# Revit family: BIM_NetShelter_SX_Series_Rack_Enclosure_21-jun-21
name_source: partatom
category: Mechanical Equipment
revit_build: Autodesk Revit 2016 (Build: 20150220_1215(x64)
units: mm (PartAtom-declared; Revit-internal decimal feet)

## family parameters
Always vertical = Yes
Cut with Voids When Loaded = No
OmniClass Number = 23.75.00.00
OmniClass Title = Climate Control (HVAC)
Part Type = Normal
Room Calculation Point = No
Round Connector Dimension = Use Diameter
Shared = No
Work Plane-Based = No

## types (28) — shared parameters
BS L5 = 774 mm
BS-L3 = 532 mm
Description = Racks and Enclosures
Front Clearance = 1000 mm  [stored 3.28084 ft]
Manufacturer = Schneider-electric
Manufacturer URL = http://www.schneider-electric.com
Model = NetShelter SX
Rear Clearance = 1000 mm  [stored 3.28084 ft]
Slot 3 = No
Top Clearance = 600 mm  [stored 1.9685 ft]
zero-valued in all types: Default Elevation

## per-type parameters (varying)
- AR3100 - NetShelter SX, 42U, 600mm Wide X 1070mm Depth: Centre Slot=Yes; Cut ref=55 mm  [stored 0.180446 ft]; Cutout 1=Yes; Cutout 2=No; Cutout Distance=590 mm  [stored 1.9357 ft]; Cutout Height=117 mm  [stored 0.383858 ft]; Cutout Width=155 mm  [stored 0.50853 ft]; Door=1911 mm; Door Radius=1419 mm; Door Width L1=431 mm  [stored 1.41404 ft]; Door1=1911 mm; Foot to Foot-H=570 mm; Foot to Foot-V=1023 mm; Handle to Handle=1092 mm; Height=1991 mm; Length=1070 mm; Net Weight of Unit=125.00 kg; Number of Small Slots L1=20; Number of small Slots L2=20; OSSS-L1=700 mm  [stored 2.29659 ft]; OSSS-L2=698 mm  [stored 2.29003 ft]; Product URL=https://www.apc.com; Side Posts=1955 mm; Slot 1=Yes; Slot 2=No; Top Roof=892 mm  [stored 2.92651 ft]; URL=http://www.schneider-electric.com; W to W-H=358 mm  [stored 1.17454 ft]; Wheel to Wheel-V=941 mm  [stored 3.08727 ft]; Width=600 mm  [stored 1.9685 ft]
- AR3307 - NetShelter SX, 48U, 600mm Wide X 1200mm Depth: Centre Slot=Yes; Cut ref=55 mm  [stored 0.180446 ft]; Cutout 1=Yes; Cutout 2=No; Cutout Distance=640 mm  [stored 2.09974 ft]; Cutout Height=200 mm  [stored 0.656168 ft]; Cutout Width=117 mm  [stored 0.383858 ft]; Door=2178 mm; Door Radius=1420 mm; Door Width L1=431 mm  [stored 1.41404 ft]; Door1=2178 mm; Foot to Foot-H=570 mm; Foot to Foot-V=1154 mm; Handle to Handle=1222 mm; Height=2258 mm; Length=1200 mm; Net Weight of Unit=149.55 kg; Number of Small Slots L1=21; Number of small Slots L2=28; OSSS-L1=760 mm; OSSS-L2=986 mm  [stored 3.23491 ft]; Product URL=https://www.apc.com; Side Posts=2222 mm; Slot 1=Yes; Slot 2=Yes; Top Roof=1021 mm  [stored 3.34974 ft]; URL=http://www.schneider-electric.com; W to W-H=358 mm  [stored 1.17454 ft]; Wheel to Wheel-V=1072 mm; Width=600 mm  [stored 1.9685 ft]
- AR3150 - NetShelter SX, 42U, 750mm Wide X 1070mm Depth: Centre Slot=Yes; Cut ref=55 mm  [stored 0.180446 ft]; Cutout 1=Yes; Cutout 2=No; Cutout Distance=600 mm  [stored 1.9685 ft]; Cutout Height=117 mm  [stored 0.383858 ft]; Cutout Width=155 mm  [stored 0.50853 ft]; Door=1911 mm; Door Radius=2586 mm; Door Width L1=581 mm  [stored 1.90617 ft]; Door1=1911 mm; Foot to Foot-H=720 mm  [stored 2.3622 ft]; Foot to Foot-V=1023 mm; Handle to Handle=1092 mm; Height=1991 mm; Length=1070 mm; Net Weight of Unit=138.23 kg; Number of Small Slots L1=20; Number of small Slots L2=20; OSSS-L1=698 mm  [stored 2.29003 ft]; OSSS-L2=840 mm  [stored 2.75591 ft]; Product URL=https://www.apc.com; Side Posts=1955 mm; Slot 1=Yes; Slot 2=No; Top Roof=892 mm  [stored 2.92651 ft]; URL=http://www.schneider-electric.com; W to W-H=508 mm; Wheel to Wheel-V=941 mm  [stored 3.08727 ft]; Width=750 mm  [stored 2.46063 ft]
- AR3105 - NetShelter SX, 45U, 600mm Wide X 1070mm Depth: Centre Slot=Yes; Cut ref=55 mm  [stored 0.180446 ft]; Cutout 1=Yes; Cutout 2=No; Cutout Distance=600 mm  [stored 1.9685 ft]; Cutout Height=117 mm  [stored 0.383858 ft]; Cutout Width=155 mm  [stored 0.50853 ft]; Door=2044 mm; Door Radius=1419 mm; Door Width L1=431 mm  [stored 1.41404 ft]; Door1=2044 mm; Foot to Foot-H=570 mm; Foot to Foot-V=1023 mm; Handle to Handle=1092 mm; Height=2124 mm; Length=1070 mm; Net Weight of Unit=137.00 kg; Number of Small Slots L1=20; Number of small Slots L2=20; OSSS-L1=693 mm  [stored 2.27362 ft]; OSSS-L2=698 mm  [stored 2.29003 ft]; Product URL=https://www.apc.com; Side Posts=2088 mm; Slot 1=Yes; Slot 2=No; Top Roof=892 mm  [stored 2.92651 ft]; URL=http://www.schneider-electric.com; W to W-H=358 mm  [stored 1.17454 ft]; Wheel to Wheel-V=941 mm  [stored 3.08727 ft]; Width=600 mm  [stored 1.9685 ft]
- AR3140 - NetShelter SX, 42U, 750mm Wide X 1070mm Depth: Centre Slot=No; Cut ref=1 mm  [stored 0.00328084 ft]; Cutout 1=No; Cutout 2=Yes; Cutout Distance=423 mm  [stored 1.3878 ft]; Cutout Height=117 mm  [stored 0.383858 ft]; Cutout Width=142 mm  [stored 0.465879 ft]; Door=1911 mm; Door Radius=2586 mm; Door Width L1=581 mm  [stored 1.90617 ft]; Door1=1911 mm; Foot to Foot-H=720 mm  [stored 2.3622 ft]; Foot to Foot-V=1023 mm; Handle to Handle=1092 mm; Height=1991 mm; Length=1070 mm; Net Weight of Unit=156.00 kg; Number of Small Slots L1=20; Number of small Slots L2=20; OSSS-L1=825 mm  [stored 2.70669 ft]; OSSS-L2=825 mm  [stored 2.70669 ft]; Product URL=https://www.apc.com; Side Posts=1955 mm; Slot 1=No; Slot 2=No; Top Roof=892 mm  [stored 2.92651 ft]; URL=http://www.schneider-electric.com; W to W-H=508 mm; Wheel to Wheel-V=941 mm  [stored 3.08727 ft]; Width=750 mm  [stored 2.46063 ft]
- AR3155 - NetShelter SX, 45U, 750mm Wide X 1070mm Depth: Centre Slot=Yes; Cut ref=55 mm  [stored 0.180446 ft]; Cutout 1=Yes; Cutout 2=No; Cutout Distance=600 mm  [stored 1.9685 ft]; Cutout Height=117 mm  [stored 0.383858 ft]; Cutout Width=155 mm  [stored 0.50853 ft]; Door=2044 mm; Door Radius=2586 mm; Door Width L1=581 mm  [stored 1.90617 ft]; Door1=2044 mm; Foot to Foot-H=720 mm  [stored 2.3622 ft]; Foot to Foot-V=1023 mm; Handle to Handle=1092 mm; Height=2124 mm; Length=1070 mm; Net Weight of Unit=155.00 kg; Number of Small Slots L1=20; Number of small Slots L2=20; OSSS-L1=710 mm; OSSS-L2=850 mm  [stored 2.78871 ft]; Product URL=https://www.apc.com; Side Posts=2088 mm; Slot 1=Yes; Slot 2=No; Top Roof=892 mm  [stored 2.92651 ft]; URL=http://www.schneider-electric.com; W to W-H=508 mm; Wheel to Wheel-V=941 mm  [stored 3.08727 ft]; Width=750 mm  [stored 2.46063 ft]
- AR3107 - NetShelter SX, 48U, 600mm Wide X 1070mm Depth: Centre Slot=Yes; Cut ref=55 mm  [stored 0.180446 ft]; Cutout 1=Yes; Cutout 2=No; Cutout Distance=600 mm  [stored 1.9685 ft]; Cutout Height=117 mm  [stored 0.383858 ft]; Cutout Width=155 mm  [stored 0.50853 ft]; Door=2178 mm; Door Radius=1419 mm; Door Width L1=431 mm  [stored 1.41404 ft]; Door1=2178 mm; Foot to Foot-H=570 mm; Foot to Foot-V=1023 mm; Handle to Handle=1092 mm; Height=2258 mm; Length=1070 mm; Net Weight of Unit=138.23 kg; Number of Small Slots L1=20; Number of small Slots L2=20; OSSS-L1=693 mm  [stored 2.27362 ft]; OSSS-L2=698 mm  [stored 2.29003 ft]; Product URL=https://www.apc.com; Side Posts=2222 mm; Slot 1=Yes; Slot 2=No; Top Roof=892 mm  [stored 2.92651 ft]; URL=http://www.schneider-electric.com; W to W-H=358 mm  [stored 1.17454 ft]; Wheel to Wheel-V=941 mm  [stored 3.08727 ft]; Width=600 mm  [stored 1.9685 ft]
- AR3157SP - NetShelter SX, 48U, 750mm Wide X 1070mm Depth: Centre Slot=Yes; Cut ref=55 mm  [stored 0.180446 ft]; Cutout 1=Yes; Cutout 2=No; Cutout Distance=600 mm  [stored 1.9685 ft]; Cutout Height=117 mm  [stored 0.383858 ft]; Cutout Width=155 mm  [stored 0.50853 ft]; Door=2178 mm; Door Radius=2586 mm; Door Width L1=581 mm  [stored 1.90617 ft]; Door1=2178 mm; Foot to Foot-H=720 mm  [stored 2.3622 ft]; Foot to Foot-V=1023 mm; Handle to Handle=1092 mm; Height=2258 mm; Length=1070 mm; Net Weight of Unit=169.00 kg; Number of Small Slots L1=20; Number of small Slots L2=20; OSSS-L1=710 mm; OSSS-L2=850 mm  [stored 2.78871 ft]; Product URL=https://www.apc.com; Side Posts=2222 mm; Slot 1=Yes; Slot 2=No; Top Roof=892 mm  [stored 2.92651 ft]; URL=http://www.schneider-electric.com; W to W-H=508 mm; Wheel to Wheel-V=941 mm  [stored 3.08727 ft]; Width=750 mm  [stored 2.46063 ft]
- AR3300 - NetShelter SX, 42U, 600mm Wide X 1200mm Depth: Centre Slot=Yes; Cut ref=55 mm  [stored 0.180446 ft]; Cutout 1=Yes; Cutout 2=No; Cutout Distance=640 mm  [stored 2.09974 ft]; Cutout Height=200 mm  [stored 0.656168 ft]; Cutout Width=117 mm  [stored 0.383858 ft]; Door=1911 mm; Door Radius=1420 mm; Door Width L1=431 mm  [stored 1.41404 ft]; Door1=1911 mm; Foot to Foot-H=570 mm; Foot to Foot-V=1154 mm; Handle to Handle=1222 mm; Height=1991 mm; Length=1200 mm; Net Weight of Unit=134.00 kg; Number of Small Slots L1=21; Number of small Slots L2=28; OSSS-L1=760 mm; OSSS-L2=986 mm  [stored 3.23491 ft]; Product URL=https://www.apc.com; Side Posts=1955 mm; Slot 1=Yes; Slot 2=Yes; Top Roof=1021 mm  [stored 3.34974 ft]; URL=http://www.schneider-electric.com; W to W-H=358 mm  [stored 1.17454 ft]; Wheel to Wheel-V=1072 mm; Width=600 mm  [stored 1.9685 ft]
- AR3305 - NetShelter SX, 45U, 600mm Wide X 1200mm Depth: Centre Slot=Yes; Cut ref=55 mm  [stored 0.180446 ft]; Cutout 1=Yes; Cutout 2=No; Cutout Distance=640 mm  [stored 2.09974 ft]; Cutout Height=200 mm  [stored 0.656168 ft]; Cutout Width=117 mm  [stored 0.383858 ft]; Door=2044 mm; Door Radius=1420 mm; Door Width L1=431 mm  [stored 1.41404 ft]; Door1=2044 mm; Foot to Foot-H=570 mm; Foot to Foot-V=1154 mm; Handle to Handle=1222 mm; Height=2124 mm; Length=1200 mm; Net Weight of Unit=141.00 kg; Number of Small Slots L1=21; Number of small Slots L2=28; OSSS-L1=760 mm; OSSS-L2=986 mm  [stored 3.23491 ft]; Product URL=https://www.apc.com; Side Posts=2088 mm; Slot 1=Yes; Slot 2=Yes; Top Roof=1021 mm  [stored 3.34974 ft]; URL=http://www.schneider-electric.com; W to W-H=358 mm  [stored 1.17454 ft]; Wheel to Wheel-V=1072 mm; Width=600 mm  [stored 1.9685 ft]
- AR3340 - NetShelter SX, 42U, 750mm Wide X 1200mm Depth: Centre Slot=No; Cut ref=1 mm  [stored 0.00328084 ft]; Cutout 1=No; Cutout 2=Yes; Cutout Distance=428 mm  [stored 1.4042 ft]; Cutout Height=240 mm  [stored 0.787402 ft]; Cutout Width=145 mm  [stored 0.475722 ft]; Door=1911 mm; Door Radius=2586 mm; Door Width L1=581 mm  [stored 1.90617 ft]; Door1=1911 mm; Foot to Foot-H=720 mm  [stored 2.3622 ft]; Foot to Foot-V=1154 mm; Handle to Handle=1222 mm; Height=1991 mm; Length=1200 mm; Net Weight of Unit=161.40 kg; Number of Small Slots L1=28; Number of small Slots L2=28; OSSS-L1=986 mm  [stored 3.23491 ft]; OSSS-L2=986 mm  [stored 3.23491 ft]; Product URL=https://www.apc.com; Side Posts=1955 mm; Slot 1=No; Slot 2=No; Top Roof=1021 mm  [stored 3.34974 ft]; URL=http://www.schneider-electric.com; W to W-H=508 mm; Wheel to Wheel-V=1072 mm; Width=750 mm  [stored 2.46063 ft]
- AR3350 - NetShelter SX, 42U, 750mm Wide X 1200mm Depth: Centre Slot=Yes; Cut ref=55 mm  [stored 0.180446 ft]; Cutout 1=Yes; Cutout 2=No; Cutout Distance=640 mm  [stored 2.09974 ft]; Cutout Height=200 mm  [stored 0.656168 ft]; Cutout Width=117 mm  [stored 0.383858 ft]; Door=1911 mm; Door Radius=2586 mm; Door Width L1=581 mm  [stored 1.90617 ft]; Door1=1911 mm; Foot to Foot-H=720 mm  [stored 2.3622 ft]; Foot to Foot-V=1154 mm; Handle to Handle=1222 mm; Height=1991 mm; Length=1200 mm; Net Weight of Unit=161.40 kg; Number of Small Slots L1=28; Number of small Slots L2=28; OSSS-L1=986 mm  [stored 3.23491 ft]; OSSS-L2=986 mm  [stored 3.23491 ft]; Product URL=https://www.apc.com; Side Posts=1955 mm; Slot 1=Yes; Slot 2=Yes; Top Roof=1021 mm  [stored 3.34974 ft]; URL=http://www.schneider-electric.com; W to W-H=508 mm; Wheel to Wheel-V=1072 mm; Width=750 mm  [stored 2.46063 ft]
- AR3355 - NetShelter SX, 45U, 750mm Wide X 1200mm Depth: Centre Slot=Yes; Cut ref=55 mm  [stored 0.180446 ft]; Cutout 1=Yes; Cutout 2=No; Cutout Distance=640 mm  [stored 2.09974 ft]; Cutout Height=200 mm  [stored 0.656168 ft]; Cutout Width=117 mm  [stored 0.383858 ft]; Door=2044 mm; Door Radius=2586 mm; Door Width L1=581 mm  [stored 1.90617 ft]; Door1=2044 mm; Foot to Foot-H=720 mm  [stored 2.3622 ft]; Foot to Foot-V=1154 mm; Handle to Handle=1222 mm; Height=2124 mm; Length=1200 mm; Net Weight of Unit=169.00 kg; Number of Small Slots L1=28; Number of small Slots L2=28; OSSS-L1=986 mm  [stored 3.23491 ft]; OSSS-L2=986 mm  [stored 3.23491 ft]; Product URL=https://www.apc.com; Side Posts=2088 mm; Slot 1=Yes; Slot 2=Yes; Top Roof=1021 mm  [stored 3.34974 ft]; URL=http://www.schneider-electric.com; W to W-H=508 mm; Wheel to Wheel-V=1072 mm; Width=750 mm  [stored 2.46063 ft]
- AR3347 - NetShelter SX, 48U, 750mm Wide X 1200mm Depth: Centre Slot=No; Cut ref=1 mm  [stored 0.00328084 ft]; Cutout 1=No; Cutout 2=Yes; Cutout Distance=428 mm  [stored 1.4042 ft]; Cutout Height=240 mm  [stored 0.787402 ft]; Cutout Width=145 mm  [stored 0.475722 ft]; Door=2178 mm; Door Radius=2586 mm; Door Width L1=581 mm  [stored 1.90617 ft]; Door1=2178 mm; Foot to Foot-H=720 mm  [stored 2.3622 ft]; Foot to Foot-V=1154 mm; Handle to Handle=1222 mm; Height=2258 mm; Length=1200 mm; Net Weight of Unit=185.00 kg; Number of Small Slots L1=28; Number of small Slots L2=28; OSSS-L1=986 mm  [stored 3.23491 ft]; OSSS-L2=986 mm  [stored 3.23491 ft]; Product URL=https://www.apc.com; Side Posts=2222 mm; Slot 1=No; Slot 2=No; Top Roof=1021 mm  [stored 3.34974 ft]; URL=http://www.schneider-electric.com; W to W-H=508 mm; Wheel to Wheel-V=1072 mm; Width=750 mm  [stored 2.46063 ft]
- AR3357 - NetShelter SX, 48U, 750mm Wide X 1200mm Depth: Centre Slot=Yes; Cut ref=55 mm  [stored 0.180446 ft]; Cutout 1=Yes; Cutout 2=No; Cutout Distance=640 mm  [stored 2.09974 ft]; Cutout Height=200 mm  [stored 0.656168 ft]; Cutout Width=117 mm  [stored 0.383858 ft]; Door=2178 mm; Door Radius=2586 mm; Door Width L1=581 mm  [stored 1.90617 ft]; Door1=2178 mm; Foot to Foot-H=720 mm  [stored 2.3622 ft]; Foot to Foot-V=1154 mm; Handle to Handle=1222 mm; Height=2258 mm; Length=1200 mm; Net Weight of Unit=169.00 kg; Number of Small Slots L1=28; Number of small Slots L2=28; OSSS-L1=986 mm  [stored 3.23491 ft]; OSSS-L2=986 mm  [stored 3.23491 ft]; Product URL=https://www.apc.com; Side Posts=2222 mm; Slot 1=Yes; Slot 2=Yes; Top Roof=1021 mm  [stored 3.34974 ft]; URL=http://www.schneider-electric.com; W to W-H=508 mm; Wheel to Wheel-V=1072 mm; Width=750 mm  [stored 2.46063 ft]
- AR3380G - NetShelter SX, 42U, 800mm Wide X 1200mm Depth: Centre Slot=Yes; Cut ref=55 mm  [stored 0.180446 ft]; Cutout 1=Yes; Cutout 2=No; Cutout Distance=640 mm  [stored 2.09974 ft]; Cutout Height=210 mm  [stored 0.688976 ft]; Cutout Width=117 mm  [stored 0.383858 ft]; Door=1911 mm; Door Radius=3048 mm; Door Width L1=631 mm  [stored 2.07021 ft]; Door1=1911 mm; Foot to Foot-H=720 mm  [stored 2.3622 ft]; Foot to Foot-V=1154 mm; Handle to Handle=1222 mm; Height=1991 mm; Length=1200 mm; Net Weight of Unit=181.50 kg; Number of Small Slots L1=28; Number of small Slots L2=28; OSSS-L1=986 mm  [stored 3.23491 ft]; OSSS-L2=986 mm  [stored 3.23491 ft]; Side Posts=1955 mm; Slot 1=Yes; Slot 2=Yes; Top Roof=1021 mm  [stored 3.34974 ft]; URL=http://www.schneider-electric.com; W to W-H=642 mm  [stored 2.1063 ft]; Wheel to Wheel-V=1072 mm; Width=800 mm  [stored 2.62467 ft]
- AR3155SP - NetShelter SX, 45U, 750mm Wide X 1070mm Depth: Centre Slot=Yes; Cut ref=55 mm  [stored 0.180446 ft]; Cutout 1=Yes; Cutout 2=No; Cutout Distance=600 mm  [stored 1.9685 ft]; Cutout Height=117 mm  [stored 0.383858 ft]; Cutout Width=155 mm  [stored 0.50853 ft]; Door=2044 mm; Door Radius=2586 mm; Door Width L1=581 mm  [stored 1.90617 ft]; Door1=2044 mm; Foot to Foot-H=720 mm  [stored 2.3622 ft]; Foot to Foot-V=1023 mm; Handle to Handle=1092 mm; Height=2124 mm; Length=1070 mm; Net Weight of Unit=155.00 kg; Number of Small Slots L1=20; Number of small Slots L2=20; OSSS-L1=710 mm; OSSS-L2=850 mm  [stored 2.78871 ft]; Side Posts=2088 mm; Slot 1=Yes; Slot 2=No; Top Roof=892 mm  [stored 2.92651 ft]; URL=http://www.schneider-electric.com; W to W-H=508 mm; Wheel to Wheel-V=941 mm  [stored 3.08727 ft]; Width=750 mm  [stored 2.46063 ft]
- AR3157 - NetShelter SX, 48U, 750mm Wide X 1070mm Depth: Centre Slot=Yes; Cut ref=55 mm  [stored 0.180446 ft]; Cutout 1=Yes; Cutout 2=No; Cutout Distance=600 mm  [stored 1.9685 ft]; Cutout Height=117 mm  [stored 0.383858 ft]; Cutout Width=155 mm  [stored 0.50853 ft]; Door=2178 mm; Door Radius=2586 mm; Door Width L1=581 mm  [stored 1.90617 ft]; Door1=2178 mm; Foot to Foot-H=720 mm  [stored 2.3622 ft]; Foot to Foot-V=1023 mm; Handle to Handle=1092 mm; Height=2258 mm; Length=1070 mm; Net Weight of Unit=169.00 kg; Number of Small Slots L1=20; Number of small Slots L2=20; OSSS-L1=710 mm; OSSS-L2=850 mm  [stored 2.78871 ft]; Product URL=https://www.apc.com; Side Posts=2222 mm; Slot 1=Yes; Slot 2=No; Top Roof=892 mm  [stored 2.92651 ft]; URL=http://www.schneider-electric.com; W to W-H=508 mm; Wheel to Wheel-V=941 mm  [stored 3.08727 ft]; Width=750 mm  [stored 2.46063 ft]
- AR3100SP - NetShelter SX, 42U, 600mm Wide X 1070mm Depth: Centre Slot=Yes; Cut ref=55 mm  [stored 0.180446 ft]; Cutout 1=Yes; Cutout 2=No; Cutout Distance=590 mm  [stored 1.9357 ft]; Cutout Height=117 mm  [stored 0.383858 ft]; Cutout Width=155 mm  [stored 0.50853 ft]; Door=1911 mm; Door Radius=1419 mm; Door Width L1=431 mm  [stored 1.41404 ft]; Door1=1911 mm; Foot to Foot-H=570 mm; Foot to Foot-V=1023 mm; Handle to Handle=1092 mm; Height=1991 mm; Length=1070 mm; Net Weight of Unit=125.00 kg; Number of Small Slots L1=20; Number of small Slots L2=20; OSSS-L1=700 mm  [stored 2.29659 ft]; OSSS-L2=698 mm  [stored 2.29003 ft]; Product URL=https://www.apc.com; Side Posts=1955 mm; Slot 1=Yes; Slot 2=No; Top Roof=892 mm  [stored 2.92651 ft]; URL=http://www.schneider-electric.com; W to W-H=358 mm  [stored 1.17454 ft]; Wheel to Wheel-V=941 mm  [stored 3.08727 ft]; Width=600 mm  [stored 1.9685 ft]
- AR3105SP - NetShelter SX, 45U, 600mm Wide X 1070mm Depth: Centre Slot=Yes; Cut ref=55 mm  [stored 0.180446 ft]; Cutout 1=Yes; Cutout 2=No; Cutout Distance=600 mm  [stored 1.9685 ft]; Cutout Height=117 mm  [stored 0.383858 ft]; Cutout Width=155 mm  [stored 0.50853 ft]; Door=2044 mm; Door Radius=1419 mm; Door Width L1=431 mm  [stored 1.41404 ft]; Door1=2044 mm; Foot to Foot-H=570 mm; Foot to Foot-V=1023 mm; Handle to Handle=1092 mm; Height=2124 mm; Length=1070 mm; Net Weight of Unit=137.00 kg; Number of Small Slots L1=20; Number of small Slots L2=20; OSSS-L1=693 mm  [stored 2.27362 ft]; OSSS-L2=698 mm  [stored 2.29003 ft]; Side Posts=2088 mm; Slot 1=Yes; Slot 2=No; Top Roof=892 mm  [stored 2.92651 ft]; URL=http://www.schneider-electric.com; W to W-H=358 mm  [stored 1.17454 ft]; Wheel to Wheel-V=941 mm  [stored 3.08727 ft]; Width=600 mm  [stored 1.9685 ft]
- AR3107SP - NetShelter SX, 48U, 600mm Wide X 1070mm Depth: Centre Slot=Yes; Cut ref=55 mm  [stored 0.180446 ft]; Cutout 1=Yes; Cutout 2=No; Cutout Distance=600 mm  [stored 1.9685 ft]; Cutout Height=117 mm  [stored 0.383858 ft]; Cutout Width=155 mm  [stored 0.50853 ft]; Door=2178 mm; Door Radius=1419 mm; Door Width L1=431 mm  [stored 1.41404 ft]; Door1=2178 mm; Foot to Foot-H=570 mm; Foot to Foot-V=1023 mm; Handle to Handle=1092 mm; Height=2258 mm; Length=1070 mm; Net Weight of Unit=138.23 kg; Number of Small Slots L1=20; Number of small Slots L2=20; OSSS-L1=693 mm  [stored 2.27362 ft]; OSSS-L2=698 mm  [stored 2.29003 ft]; Product URL=https://www.apc.com; Side Posts=2222 mm; Slot 1=Yes; Slot 2=No; Top Roof=892 mm  [stored 2.92651 ft]; URL=http://www.schneider-electric.com; W to W-H=358 mm  [stored 1.17454 ft]; Wheel to Wheel-V=941 mm  [stored 3.08727 ft]; Width=600 mm  [stored 1.9685 ft]
- AR3150SP - NetShelter SX, 42U, 750mm Wide X 1070mm Depth: Centre Slot=Yes; Cut ref=55 mm  [stored 0.180446 ft]; Cutout 1=Yes; Cutout 2=No; Cutout Distance=600 mm  [stored 1.9685 ft]; Cutout Height=117 mm  [stored 0.383858 ft]; Cutout Width=155 mm  [stored 0.50853 ft]; Door=1911 mm; Door Radius=2586 mm; Door Width L1=581 mm  [stored 1.90617 ft]; Door1=1911 mm; Foot to Foot-H=720 mm  [stored 2.3622 ft]; Foot to Foot-V=1023 mm; Handle to Handle=1092 mm; Height=1991 mm; Length=1070 mm; Net Weight of Unit=138.23 kg; Number of Small Slots L1=20; Number of small Slots L2=20; OSSS-L1=698 mm  [stored 2.29003 ft]; OSSS-L2=840 mm  [stored 2.75591 ft]; Product URL=https://www.apc.com; Side Posts=1955 mm; Slot 1=Yes; Slot 2=No; Top Roof=892 mm  [stored 2.92651 ft]; URL=http://www.schneider-electric.com; W to W-H=508 mm; Wheel to Wheel-V=941 mm  [stored 3.08727 ft]; Width=750 mm  [stored 2.46063 ft]
- AR3300SP - NetShelter SX, 42U, 600mm Wide X 1200mm Depth: Centre Slot=Yes; Cut ref=55 mm  [stored 0.180446 ft]; Cutout 1=Yes; Cutout 2=No; Cutout Distance=640 mm  [stored 2.09974 ft]; Cutout Height=200 mm  [stored 0.656168 ft]; Cutout Width=117 mm  [stored 0.383858 ft]; Door=1911 mm; Door Radius=1420 mm; Door Width L1=431 mm  [stored 1.41404 ft]; Door1=1911 mm; Foot to Foot-H=570 mm; Foot to Foot-V=1154 mm; Handle to Handle=1222 mm; Height=1991 mm; Length=1200 mm; Net Weight of Unit=134.00 kg; Number of Small Slots L1=21; Number of small Slots L2=28; OSSS-L1=760 mm; OSSS-L2=986 mm  [stored 3.23491 ft]; Product URL=https://www.apc.com; Side Posts=1955 mm; Slot 1=Yes; Slot 2=Yes; Top Roof=1021 mm  [stored 3.34974 ft]; URL=http://www.schneider-electric.com; W to W-H=358 mm  [stored 1.17454 ft]; Wheel to Wheel-V=1072 mm; Width=600 mm  [stored 1.9685 ft]
- AR3305SP - NetShelter SX, 45U, 600mm Wide X 1200mm Depth: Centre Slot=Yes; Cut ref=55 mm  [stored 0.180446 ft]; Cutout 1=Yes; Cutout 2=No; Cutout Distance=640 mm  [stored 2.09974 ft]; Cutout Height=200 mm  [stored 0.656168 ft]; Cutout Width=117 mm  [stored 0.383858 ft]; Door=2044 mm; Door Radius=1420 mm; Door Width L1=431 mm  [stored 1.41404 ft]; Door1=2044 mm; Foot to Foot-H=570 mm; Foot to Foot-V=1154 mm; Handle to Handle=1222 mm; Height=2124 mm; Length=1200 mm; Net Weight of Unit=141.00 kg; Number of Small Slots L1=21; Number of small Slots L2=28; OSSS-L1=760 mm; OSSS-L2=986 mm  [stored 3.23491 ft]; Side Posts=2088 mm; Slot 1=Yes; Slot 2=Yes; Top Roof=1021 mm  [stored 3.34974 ft]; URL=http://www.schneider-electric.com; W to W-H=358 mm  [stored 1.17454 ft]; Wheel to Wheel-V=1072 mm; Width=600 mm  [stored 1.9685 ft]
- AR3307SP - NetShelter SX, 48U, 600mm Wide X 1200mm Depth: Centre Slot=Yes; Cut ref=55 mm  [stored 0.180446 ft]; Cutout 1=Yes; Cutout 2=No; Cutout Distance=640 mm  [stored 2.09974 ft]; Cutout Height=200 mm  [stored 0.656168 ft]; Cutout Width=117 mm  [stored 0.383858 ft]; Door=2178 mm; Door Radius=1420 mm; Door Width L1=431 mm  [stored 1.41404 ft]; Door1=2178 mm; Foot to Foot-H=570 mm; Foot to Foot-V=1154 mm; Handle to Handle=1222 mm; Height=2258 mm; Length=1200 mm; Net Weight of Unit=149.55 kg; Number of Small Slots L1=21; Number of small Slots L2=28; OSSS-L1=760 mm; OSSS-L2=986 mm  [stored 3.23491 ft]; Product URL=https://www.apc.com; Side Posts=2222 mm; Slot 1=Yes; Slot 2=Yes; Top Roof=1021 mm  [stored 3.34974 ft]; URL=http://www.schneider-electric.com; W to W-H=358 mm  [stored 1.17454 ft]; Wheel to Wheel-V=1072 mm; Width=600 mm  [stored 1.9685 ft]
- AR3350SP - NetShelter SX, 42U, 750mm Wide X 1200mm Depth: Centre Slot=Yes; Cut ref=55 mm  [stored 0.180446 ft]; Cutout 1=Yes; Cutout 2=No; Cutout Distance=640 mm  [stored 2.09974 ft]; Cutout Height=200 mm  [stored 0.656168 ft]; Cutout Width=117 mm  [stored 0.383858 ft]; Door=1911 mm; Door Radius=2586 mm; Door Width L1=581 mm  [stored 1.90617 ft]; Door1=1911 mm; Foot to Foot-H=720 mm  [stored 2.3622 ft]; Foot to Foot-V=1154 mm; Handle to Handle=1222 mm; Height=1991 mm; Length=1200 mm; Net Weight of Unit=161.40 kg; Number of Small Slots L1=28; Number of small Slots L2=28; OSSS-L1=986 mm  [stored 3.23491 ft]; OSSS-L2=986 mm  [stored 3.23491 ft]; Product URL=https://www.apc.com; Side Posts=1955 mm; Slot 1=Yes; Slot 2=Yes; Top Roof=1021 mm  [stored 3.34974 ft]; URL=http://www.schneider-electric.com; W to W-H=508 mm; Wheel to Wheel-V=1072 mm; Width=750 mm  [stored 2.46063 ft]
- AR3355SP - NetShelter SX, 45U, 750mm Wide X 1200mm Depth: Centre Slot=Yes; Cut ref=55 mm  [stored 0.180446 ft]; Cutout 1=Yes; Cutout 2=No; Cutout Distance=640 mm  [stored 2.09974 ft]; Cutout Height=200 mm  [stored 0.656168 ft]; Cutout Width=117 mm  [stored 0.383858 ft]; Door=2044 mm; Door Radius=2586 mm; Door Width L1=581 mm  [stored 1.90617 ft]; Door1=2044 mm; Foot to Foot-H=720 mm  [stored 2.3622 ft]; Foot to Foot-V=1154 mm; Handle to Handle=1222 mm; Height=2124 mm; Length=1200 mm; Net Weight of Unit=169.00 kg; Number of Small Slots L1=28; Number of small Slots L2=28; OSSS-L1=986 mm  [stored 3.23491 ft]; OSSS-L2=986 mm  [stored 3.23491 ft]; Side Posts=2088 mm; Slot 1=Yes; Slot 2=Yes; Top Roof=1021 mm  [stored 3.34974 ft]; URL=http://www.schneider-electric.com; W to W-H=508 mm; Wheel to Wheel-V=1072 mm; Width=750 mm  [stored 2.46063 ft]
- AR3387 - NetShelter SX, 48U, 800mm Wide x 1200mm Depth: Centre Slot=Yes; Cut ref=55 mm  [stored 0.180446 ft]; Cutout 1=Yes; Cutout 2=No; Cutout Distance=640 mm  [stored 2.09974 ft]; Cutout Height=210 mm  [stored 0.688976 ft]; Cutout Width=117 mm  [stored 0.383858 ft]; Door=2178 mm; Door Radius=3048 mm; Door Width L1=631 mm  [stored 2.07021 ft]; Door1=2178 mm; Foot to Foot-H=720 mm  [stored 2.3622 ft]; Foot to Foot-V=1154 mm; Handle to Handle=1222 mm; Height=2258 mm; Length=1200 mm; Net Weight of Unit=200.50 kg; Number of Small Slots L1=28; Number of small Slots L2=28; OSSS-L1=986 mm  [stored 3.23491 ft]; OSSS-L2=986 mm  [stored 3.23491 ft]; Side Posts=2222 mm; Slot 1=Yes; Slot 2=Yes; Top Roof=1021 mm  [stored 3.34974 ft]; URL=https://www.apc.com; W to W-H=642 mm  [stored 2.1063 ft]; Wheel to Wheel-V=1072 mm; Width=800 mm  [stored 2.62467 ft]

note: [stored X ft] marks values corroborated as IEEE doubles in the binary element streams (Revit-internal decimal feet)

## geometry (parser evidence)
native form markers: Blend x4, Sweep x16
no freeform markers — native parametric forms only
